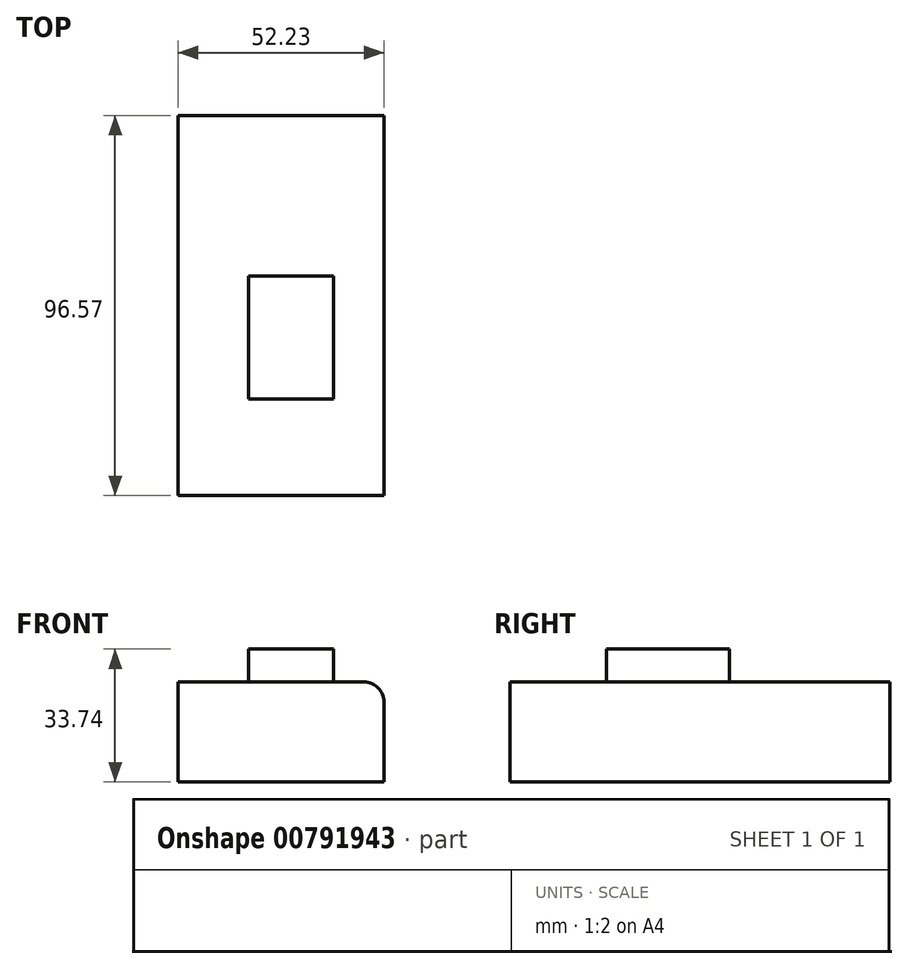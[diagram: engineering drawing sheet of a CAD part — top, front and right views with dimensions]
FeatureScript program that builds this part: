
annotation { "Feature Type Name" : "Feature", "Feature Type Description" : "" }
export const myFeature = defineFeature(function(context is Context, id is Id, definition is map)
    precondition{}
    {
        {
            var Q0;
            Q0=qCreatedBy(makeId("Top.planeOp"),FACE);
            var sketch = newSketch(context, id + "F0", { "sketchPlane" : qUnion([Q0])});
            skLineSegment(sketch, "E0.bottom", {"start": v(0, -49.77) * mm, "end": v(52.23, -49.77) * mm});
            skLineSegment(sketch, "E0.top", {"start": v(0, 46.8) * mm, "end": v(52.23, 46.8) * mm});
            skLineSegment(sketch, "E0.left", {"start": v(0, -49.77) * mm, "end": v(0, 46.8) * mm});
            skLineSegment(sketch, "E0.right", {"start": v(52.23, -49.77) * mm, "end": v(52.23, 46.8) * mm});
            skSolve(sketch);
        }
        {
            var Q0;
            Q0 = qSketchRegion(id + "F0", true);
            extrude(context, id + "F1", {"entities" : qUnion([Q0]), "depth" : 25.4 * mm, "offsetDistance" : 25.4 * mm});
        }
        {
            var Q0;
            Q0=makeQuery(id+"F1.opExtrude","CAP_EDGE",EDGE,{"disambiguationData":[OSD([sQuery(id+"F0.wireOp",EDGE,"E0.right")])],"isStart":false});
            fillet(context, id + "F2", {"entities" : qUnion([Q0]), "radius" : 5.08 * mm, "tangentPropagation" : true, "allowEdgeOverflow" : false});
        }
        {
            var Q0;
            Q0=makeQuery(id+"F1.opExtrude","CAP_FACE",FACE,{"disambiguationData":[OSD([sQuery(id+"F0.wireOp",EDGE,"E0.bottom"),sQuery(id+"F0.wireOp",EDGE,"E0.top"),sQuery(id+"F0.wireOp",EDGE,"E0.left"),sQuery(id+"F0.wireOp",EDGE,"E0.right")])],"isStart":false});
            var sketch = newSketch(context, id + "F3", { "sketchPlane" : qUnion([Q0])});
            skLineSegment(sketch, "E1.bottom", {"start": v(17.84, -25.18) * mm, "end": v(39.46, -25.18) * mm});
            skLineSegment(sketch, "E1.top", {"start": v(17.84, 6) * mm, "end": v(39.46, 6) * mm});
            skLineSegment(sketch, "E1.left", {"start": v(17.84, -25.18) * mm, "end": v(17.84, 6) * mm});
            skLineSegment(sketch, "E1.right", {"start": v(39.46, -25.18) * mm, "end": v(39.46, 6) * mm});
            skLineSegment(sketch, "E2.bottom", {"start": v(92.72, -6.06) * mm, "end": v(94.89, -6.06) * mm});
            skLineSegment(sketch, "E2.top", {"start": v(92.72, -3.9) * mm, "end": v(94.89, -3.9) * mm});
            skLineSegment(sketch, "E2.left", {"start": v(92.72, -6.06) * mm, "end": v(92.72, -3.9) * mm});
            skLineSegment(sketch, "E2.right", {"start": v(94.89, -6.06) * mm, "end": v(94.89, -3.9) * mm});
            skSolve(sketch);
        }
        {
            var Q0;
            Q0=makeQuery(id+"F3.imprint","IMPRINT",FACE,{"disambiguationData":[TD([[makeQuery(id+"F3.imprint","IMPRINT",EDGE,{"derivedFrom":sQuery(id+"F3.wireOp",EDGE,"E1.bottom")}),1.0]])]});
            extrude(context, id + "F4", {"entities" : qUnion([Q0]), "operationType" : NewBodyOperationType.ADD, "depth" : 8.34 * mm, "offsetDistance" : 25.4 * mm});
        }
    });
